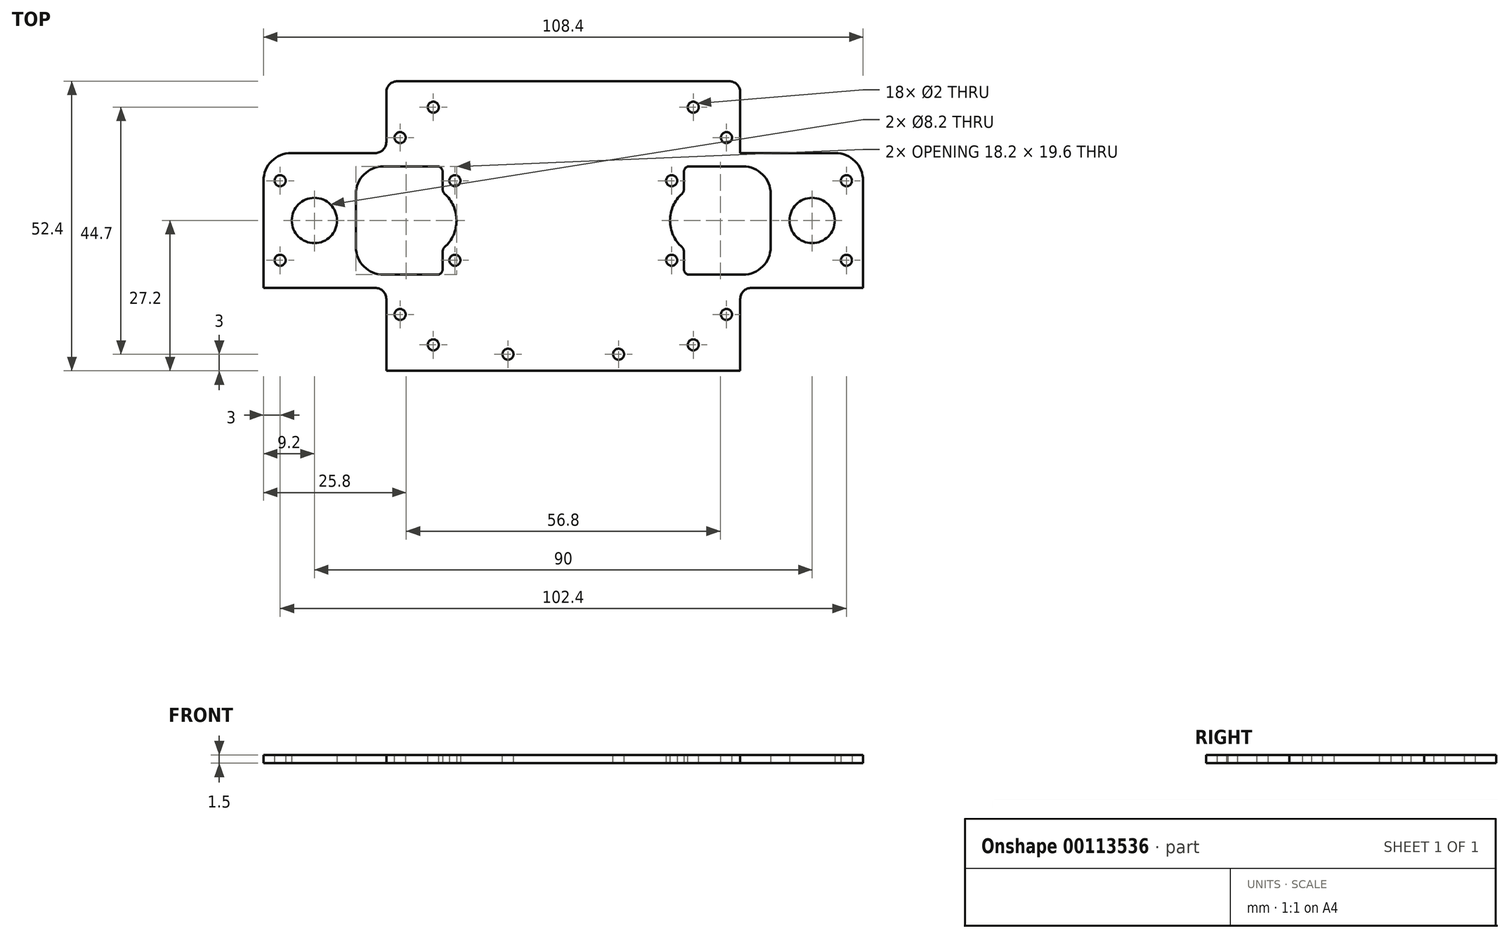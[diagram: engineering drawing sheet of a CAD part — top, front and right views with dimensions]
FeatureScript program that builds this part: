
annotation { "Feature Type Name" : "Feature", "Feature Type Description" : "" }
export const myFeature = defineFeature(function(context is Context, id is Id, definition is map)
    precondition{}
    {
        {
            var Q0;
            Q0=qCreatedBy(makeId("Top.planeOp"),FACE);
            var sketch = newSketch(context, id + "F0", { "sketchPlane" : qUnion([Q0])});
            skLineSegment(sketch, "E0.bottom", {"start": v(54.2, -12.2) * mm, "end": v(-54.2, -12.2) * mm});
            skLineSegment(sketch, "E0.top", {"start": v(54.2, 12.2) * mm, "end": v(-54.2, 12.2) * mm});
            skLineSegment(sketch, "E0.left", {"start": v(54.2, -12.2) * mm, "end": v(54.2, 12.2) * mm});
            skLineSegment(sketch, "E0.right", {"start": v(-54.2, -12.2) * mm, "end": v(-54.2, 12.2) * mm});
            skPoint(sketch, "E0.middle", {"position": v(0, 0) * mm});
            skCircle(sketch, "E1", {"center": v(-45, 0) * mm, "radius": 4.1 * mm});
            skCircle(sketch, "E2", {"center": v(-51.2, 7.2) * mm, "radius": 1 * mm});
            skCircle(sketch, "E3", {"center": v(-19.6, 7.2) * mm, "radius": 1 * mm});
            skLineSegment(sketch, "E4.bottom", {"start": v(-32.5, 9.8) * mm, "end": v(-22.8, 9.8) * mm});
            skLineSegment(sketch, "E4.top", {"start": v(-32.5, -9.8) * mm, "end": v(-22.8, -9.8) * mm});
            skLineSegment(sketch, "E4.left", {"start": v(-37.5, 4.8) * mm, "end": v(-37.5, -4.8) * mm});
            skLineSegment(sketch, "E4.right", {"start": v(-21.8, 8.8) * mm, "end": v(-21.8, 5.6) * mm});
            skPoint(sketch, "E4.middle", {"position": v(-29.65, 0) * mm});
            skPoint(sketch, "E5.visualSharp", {"position": v(-37.5, 9.8) * mm});
            skArc(sketch, "E5.filletArc", {"start": v(-32.5, 9.8) * mm, "mid": v(-36.04, 8.34) * mm, "end": v(-37.5, 4.8) * mm});
            skPoint(sketch, "E6.visualSharp", {"position": v(-37.5, -9.8) * mm});
            skArc(sketch, "E6.filletArc", {"start": v(-37.5, -4.8) * mm, "mid": v(-36.04, -8.34) * mm, "end": v(-32.5, -9.8) * mm});
            skPoint(sketch, "E7.visualSharp", {"position": v(-21.8, 9.8) * mm});
            skArc(sketch, "E7.filletArc", {"start": v(-21.8, 8.8) * mm, "mid": v(-22.1, 9.5) * mm, "end": v(-22.8, 9.8) * mm});
            skPoint(sketch, "E8.visualSharp", {"position": v(-21.8, -9.8) * mm});
            skArc(sketch, "E8.filletArc", {"start": v(-22.8, -9.8) * mm, "mid": v(-22.1, -9.5) * mm, "end": v(-21.8, -8.8) * mm});
            skCircle(sketch, "E9.MirrorC", {"center": v(-51.2, -7.2) * mm, "radius": 1 * mm});
            skCircle(sketch, "E10.MirrorC", {"center": v(-19.6, -7.2) * mm, "radius": 1 * mm});
            skArc(sketch, "E11.MirrorCS", {"start": v(21.8, 8.8) * mm, "mid": v(22.1, 9.5) * mm, "end": v(22.8, 9.8) * mm});
            skArc(sketch, "E12.MirrorCS", {"start": v(22.8, -9.8) * mm, "mid": v(22.1, -9.5) * mm, "end": v(21.8, -8.8) * mm});
            skCircle(sketch, "E13.MirrorC", {"center": v(19.6, -7.2) * mm, "radius": 1 * mm});
            skArc(sketch, "E14.MirrorCS", {"start": v(37.5, -4.8) * mm, "mid": v(36.04, -8.34) * mm, "end": v(32.5, -9.8) * mm});
            skArc(sketch, "E15.MirrorCS", {"start": v(32.5, 9.8) * mm, "mid": v(36.04, 8.34) * mm, "end": v(37.5, 4.8) * mm});
            skLineSegment(sketch, "E16.MirrorCS", {"start": v(21.8, 8.8) * mm, "end": v(21.8, 5.6) * mm});
            skPoint(sketch, "E17.MirrorP", {"position": v(21.8, -9.8) * mm});
            skLineSegment(sketch, "E18.MirrorCS", {"start": v(32.5, 9.8) * mm, "end": v(22.8, 9.8) * mm});
            skCircle(sketch, "E19.MirrorC", {"center": v(19.6, 7.2) * mm, "radius": 1 * mm});
            skPoint(sketch, "E20.MirrorP", {"position": v(21.8, 9.8) * mm});
            skPoint(sketch, "E21.MirrorP", {"position": v(29.65, 0) * mm});
            skCircle(sketch, "E22.MirrorC", {"center": v(51.2, -7.2) * mm, "radius": 1 * mm});
            skCircle(sketch, "E23.MirrorC", {"center": v(51.2, 7.2) * mm, "radius": 1 * mm});
            skCircle(sketch, "E24.MirrorC", {"center": v(45, 0) * mm, "radius": 4.1 * mm});
            skLineSegment(sketch, "E25.MirrorCS", {"start": v(37.5, 4.8) * mm, "end": v(37.5, -4.8) * mm});
            skPoint(sketch, "E26.MirrorP", {"position": v(37.5, -9.8) * mm});
            skLineSegment(sketch, "E27.MirrorCS", {"start": v(32.5, -9.8) * mm, "end": v(22.8, -9.8) * mm});
            skPoint(sketch, "E28.MirrorP", {"position": v(37.5, 9.8) * mm});
            skArc(sketch, "E29", {"start": v(-21.47, -4.84) * mm, "mid": v(-19.3, 0) * mm, "end": v(-21.47, 4.84) * mm});
            skLineSegment(sketch, "E30.trimOffspring", {"start": v(-21.8, -5.6) * mm, "end": v(-21.8, -8.8) * mm});
            skPoint(sketch, "E31.visualSharp", {"position": v(-21.8, 5.12) * mm});
            skArc(sketch, "E31.filletArc", {"start": v(-21.8, 5.6) * mm, "mid": v(-21.71, 5.18) * mm, "end": v(-21.47, 4.84) * mm});
            skPoint(sketch, "E32.visualSharp", {"position": v(-21.8, -5.12) * mm});
            skArc(sketch, "E32.filletArc", {"start": v(-21.47, -4.84) * mm, "mid": v(-21.71, -5.18) * mm, "end": v(-21.8, -5.6) * mm});
            skArc(sketch, "E33.MirrorCS", {"start": v(21.8, 5.6) * mm, "mid": v(21.71, 5.18) * mm, "end": v(21.47, 4.84) * mm});
            skArc(sketch, "E34.MirrorCS", {"start": v(21.47, -4.84) * mm, "mid": v(19.3, 0) * mm, "end": v(21.47, 4.84) * mm});
            skPoint(sketch, "E35.MirrorP", {"position": v(21.8, 5.12) * mm});
            skPoint(sketch, "E36.MirrorP", {"position": v(21.8, -5.12) * mm});
            skArc(sketch, "E37.MirrorCS", {"start": v(21.47, -4.84) * mm, "mid": v(21.71, -5.18) * mm, "end": v(21.8, -5.6) * mm});
            skLineSegment(sketch, "E38.trimOffspring", {"start": v(21.8, -5.6) * mm, "end": v(21.8, -8.8) * mm});
            skSolve(sketch);
        }
        {
            var Q0;
            Q0=qSketchRegion(id+"F0",true);
            extrude(context, id + "F1", {"entities" : qUnion([Q0]), "depth" : 1.5 * mm});
        }
        {
            var Q0;
            Q0=makeQuery(id+"F1.opExtrude","SWEPT_FACE",FACE,{"disambiguationData":[OSD([sQuery(id+"F0.wireOp",EDGE,"E0.bottom")])]});
            var sketch = newSketch(context, id + "F2", { "sketchPlane" : qUnion([Q0])});
            skLineSegment(sketch, "E39.bottom", {"start": v(-54.2, 1.5) * mm, "end": v(54.2, 1.5) * mm});
            skLineSegment(sketch, "E39.top", {"start": v(-54.2, 0) * mm, "end": v(54.2, 0) * mm});
            skLineSegment(sketch, "E39.left", {"start": v(-54.2, 1.5) * mm, "end": v(-54.2, 0) * mm});
            skLineSegment(sketch, "E39.right", {"start": v(54.2, 1.5) * mm, "end": v(54.2, 0) * mm});
            skSolve(sketch);
        }
        {
            var Q0;
            Q0=qSketchRegion(id+"F2",true);
            extrude(context, id + "F3", {"entities" : qUnion([Q0]), "operationType" : NewBodyOperationType.ADD, "depth" : 15 * mm});
        }
        {
            var Q0;
            Q0=makeQuery(id+"F3.boolean.opBoolean","MERGE",FACE,{"derivedFrom":[makeQuery(id+"F1.opExtrude","CAP_FACE",FACE,{"disambiguationData":[OSD([sQuery(id+"F0.wireOp",EDGE,"E0.bottom"),sQuery(id+"F0.wireOp",EDGE,"E0.top"),sQuery(id+"F0.wireOp",EDGE,"E0.left"),sQuery(id+"F0.wireOp",EDGE,"E0.right"),sQuery(id+"F0.wireOp",EDGE,"E1"),sQuery(id+"F0.wireOp",EDGE,"E2"),sQuery(id+"F0.wireOp",EDGE,"E3"),sQuery(id+"F0.wireOp",EDGE,"E4.bottom"),sQuery(id+"F0.wireOp",EDGE,"E4.top"),sQuery(id+"F0.wireOp",EDGE,"E4.left"),sQuery(id+"F0.wireOp",EDGE,"E4.right"),sQuery(id+"F0.wireOp",EDGE,"E5.filletArc"),sQuery(id+"F0.wireOp",EDGE,"E6.filletArc"),sQuery(id+"F0.wireOp",EDGE,"E7.filletArc"),sQuery(id+"F0.wireOp",EDGE,"E8.filletArc"),sQuery(id+"F0.wireOp",EDGE,"E9.MirrorC"),sQuery(id+"F0.wireOp",EDGE,"E10.MirrorC"),sQuery(id+"F0.wireOp",EDGE,"E11.MirrorCS"),sQuery(id+"F0.wireOp",EDGE,"E12.MirrorCS"),sQuery(id+"F0.wireOp",EDGE,"E13.MirrorC"),sQuery(id+"F0.wireOp",EDGE,"E14.MirrorCS"),sQuery(id+"F0.wireOp",EDGE,"E15.MirrorCS"),sQuery(id+"F0.wireOp",EDGE,"E16.MirrorCS"),sQuery(id+"F0.wireOp",EDGE,"E18.MirrorCS"),sQuery(id+"F0.wireOp",EDGE,"E19.MirrorC"),sQuery(id+"F0.wireOp",EDGE,"E22.MirrorC"),sQuery(id+"F0.wireOp",EDGE,"E23.MirrorC"),sQuery(id+"F0.wireOp",EDGE,"E24.MirrorC"),sQuery(id+"F0.wireOp",EDGE,"E25.MirrorCS"),sQuery(id+"F0.wireOp",EDGE,"E27.MirrorCS"),sQuery(id+"F0.wireOp",EDGE,"E29"),sQuery(id+"F0.wireOp",EDGE,"E30.trimOffspring"),sQuery(id+"F0.wireOp",EDGE,"E31.filletArc"),sQuery(id+"F0.wireOp",EDGE,"E32.filletArc"),sQuery(id+"F0.wireOp",EDGE,"E33.MirrorCS"),sQuery(id+"F0.wireOp",EDGE,"E34.MirrorCS"),sQuery(id+"F0.wireOp",EDGE,"E37.MirrorCS"),sQuery(id+"F0.wireOp",EDGE,"E38.trimOffspring")])],"isStart":false}),makeQuery(id+"F3.opExtrude","SWEPT_FACE",FACE,{"disambiguationData":[OSD([sQuery(id+"F2.wireOp",EDGE,"E39.bottom")])]})]});
            var sketch = newSketch(context, id + "F4", { "sketchPlane" : qUnion([Q0])});
            skLineSegment(sketch, "E40.bottom", {"start": v(-54.2, -27.2) * mm, "end": v(-32, -27.2) * mm});
            skLineSegment(sketch, "E40.top", {"start": v(-54.2, -12.2) * mm, "end": v(-32, -12.2) * mm});
            skLineSegment(sketch, "E40.left", {"start": v(-54.2, -27.2) * mm, "end": v(-54.2, -12.2) * mm});
            skLineSegment(sketch, "E40.right", {"start": v(-32, -27.2) * mm, "end": v(-32, -12.2) * mm});
            skPoint(sketch, "E41", {"position": v(-19.6, -7.2) * mm});
            skLineSegment(sketch, "E42.MirrorCS", {"start": v(54.2, -27.2) * mm, "end": v(32, -27.2) * mm});
            skLineSegment(sketch, "E43.MirrorCS", {"start": v(54.2, -12.2) * mm, "end": v(32, -12.2) * mm});
            skLineSegment(sketch, "E44.MirrorCS", {"start": v(54.2, -27.2) * mm, "end": v(54.2, -12.2) * mm});
            skLineSegment(sketch, "E45.MirrorCS", {"start": v(32, -27.2) * mm, "end": v(32, -12.2) * mm});
            skSolve(sketch);
        }
        {
            var Q0;
            Q0=qSketchRegion(id+"F4",true);
            extrude(context, id + "F5", {"entities" : qUnion([Q0]), "operationType" : NewBodyOperationType.REMOVE, "endBound" : BoundingType.UP_TO_NEXT, "oppositeDirection" : true, "depth" : 25 * mm});
        }
        {
            var Q0;
            Q0=makeQuery(id+"F3.boolean.opBoolean","MERGE",FACE,{"derivedFrom":[makeQuery(id+"F1.opExtrude","CAP_FACE",FACE,{"disambiguationData":[OSD([sQuery(id+"F0.wireOp",EDGE,"E0.bottom"),sQuery(id+"F0.wireOp",EDGE,"E0.top"),sQuery(id+"F0.wireOp",EDGE,"E0.left"),sQuery(id+"F0.wireOp",EDGE,"E0.right"),sQuery(id+"F0.wireOp",EDGE,"E1"),sQuery(id+"F0.wireOp",EDGE,"E2"),sQuery(id+"F0.wireOp",EDGE,"E3"),sQuery(id+"F0.wireOp",EDGE,"E4.bottom"),sQuery(id+"F0.wireOp",EDGE,"E4.top"),sQuery(id+"F0.wireOp",EDGE,"E4.left"),sQuery(id+"F0.wireOp",EDGE,"E4.right"),sQuery(id+"F0.wireOp",EDGE,"E5.filletArc"),sQuery(id+"F0.wireOp",EDGE,"E6.filletArc"),sQuery(id+"F0.wireOp",EDGE,"E7.filletArc"),sQuery(id+"F0.wireOp",EDGE,"E8.filletArc"),sQuery(id+"F0.wireOp",EDGE,"E9.MirrorC"),sQuery(id+"F0.wireOp",EDGE,"E10.MirrorC"),sQuery(id+"F0.wireOp",EDGE,"E11.MirrorCS"),sQuery(id+"F0.wireOp",EDGE,"E12.MirrorCS"),sQuery(id+"F0.wireOp",EDGE,"E13.MirrorC"),sQuery(id+"F0.wireOp",EDGE,"E14.MirrorCS"),sQuery(id+"F0.wireOp",EDGE,"E15.MirrorCS"),sQuery(id+"F0.wireOp",EDGE,"E16.MirrorCS"),sQuery(id+"F0.wireOp",EDGE,"E18.MirrorCS"),sQuery(id+"F0.wireOp",EDGE,"E19.MirrorC"),sQuery(id+"F0.wireOp",EDGE,"E22.MirrorC"),sQuery(id+"F0.wireOp",EDGE,"E23.MirrorC"),sQuery(id+"F0.wireOp",EDGE,"E24.MirrorC"),sQuery(id+"F0.wireOp",EDGE,"E25.MirrorCS"),sQuery(id+"F0.wireOp",EDGE,"E27.MirrorCS"),sQuery(id+"F0.wireOp",EDGE,"E29"),sQuery(id+"F0.wireOp",EDGE,"E30.trimOffspring"),sQuery(id+"F0.wireOp",EDGE,"E31.filletArc"),sQuery(id+"F0.wireOp",EDGE,"E32.filletArc"),sQuery(id+"F0.wireOp",EDGE,"E33.MirrorCS"),sQuery(id+"F0.wireOp",EDGE,"E34.MirrorCS"),sQuery(id+"F0.wireOp",EDGE,"E37.MirrorCS"),sQuery(id+"F0.wireOp",EDGE,"E38.trimOffspring")])],"isStart":false}),makeQuery(id+"F3.opExtrude","SWEPT_FACE",FACE,{"disambiguationData":[OSD([sQuery(id+"F2.wireOp",EDGE,"E39.bottom")])]})]});
            var sketch = newSketch(context, id + "F6", { "sketchPlane" : qUnion([Q0])});
            skLineSegment(sketch, "E46.bottom", {"start": v(-32, -27.2) * mm, "end": v(32, -27.2) * mm, "construction": true});
            skLineSegment(sketch, "E46.top", {"start": v(-32, 12.2) * mm, "end": v(32, 12.2) * mm, "construction": true});
            skLineSegment(sketch, "E46.left", {"start": v(-32, -27.2) * mm, "end": v(-32, 12.2) * mm, "construction": true});
            skLineSegment(sketch, "E46.right", {"start": v(32, -27.2) * mm, "end": v(32, 12.2) * mm, "construction": true});
            skLineSegment(sketch, "E47", {"start": v(-32, -12.2) * mm, "end": v(32, -12.2) * mm, "construction": true});
            skCircle(sketch, "E48", {"center": v(-23.5, -33.7) * mm, "radius": 1 * mm, "construction": true});
            skCircle(sketch, "E49.MirrorC", {"center": v(-23.5, 9.3) * mm, "radius": 1 * mm, "construction": true});
            skCircle(sketch, "E50.MirrorC", {"center": v(23.5, 9.3) * mm, "radius": 1 * mm, "construction": true});
            skCircle(sketch, "E51.MirrorC", {"center": v(23.5, -33.7) * mm, "radius": 1 * mm, "construction": true});
            skCircle(sketch, "E52", {"center": v(-10, -24.2) * mm, "radius": 1 * mm});
            skCircle(sketch, "E53.MirrorC", {"center": v(10, -24.2) * mm, "radius": 1 * mm});
            skSolve(sketch);
        }
        {
            var Q0;
            Q0=makeQuery(id+"F5.boolean.opBoolean","COPY",EDGE,{"derivedFrom":makeQuery(id+"F5.opExtrude","SWEPT_EDGE",EDGE,{"disambiguationData":[OSD([sQuery(id+"F4.wireOp",EDGE,"E40.top"),sQuery(id+"F4.wireOp",EDGE,"E40.right")])]})});
            var Q1;
            Q1=makeQuery(id+"F5.boolean.opBoolean","COPY",EDGE,{"derivedFrom":makeQuery(id+"F5.opExtrude","SWEPT_EDGE",EDGE,{"disambiguationData":[OSD([sQuery(id+"F4.wireOp",EDGE,"E43.MirrorCS"),sQuery(id+"F4.wireOp",EDGE,"E45.MirrorCS")])]})});
            fillet(context, id + "F7", {"entities" : qUnion([Q0, Q1]), "radius" : 2 * mm, "tangentPropagation" : true, "allowEdgeOverflow" : false});
        }
        {
            var Q0;
            Q0=makeQuery(id+"F1.opExtrude","SWEPT_EDGE",EDGE,{"disambiguationData":[OSD([sQuery(id+"F0.wireOp",EDGE,"E0.top"),sQuery(id+"F0.wireOp",EDGE,"E0.right")])]});
            var Q1;
            Q1=makeQuery(id+"F5.boolean.opBoolean","COPY",EDGE,{"derivedFrom":makeQuery(id+"F5.opExtrude","SWEPT_EDGE",EDGE,{"disambiguationData":[OSD([sQuery(id+"F0.wireOp",EDGE,"E0.right"),sQuery(id+"F2.wireOp",EDGE,"E39.bottom"),sQuery(id+"F2.wireOp",EDGE,"E39.left"),sQuery(id+"F4.wireOp",EDGE,"E40.top"),sQuery(id+"F4.wireOp",EDGE,"E40.left")])]})});
            var Q2;
            Q2=makeQuery(id+"F1.opExtrude","SWEPT_EDGE",EDGE,{"disambiguationData":[OSD([sQuery(id+"F0.wireOp",EDGE,"E0.top"),sQuery(id+"F0.wireOp",EDGE,"E0.left")])]});
            var Q3;
            Q3=makeQuery(id+"F5.boolean.opBoolean","COPY",EDGE,{"derivedFrom":makeQuery(id+"F5.opExtrude","SWEPT_EDGE",EDGE,{"disambiguationData":[OSD([sQuery(id+"F0.wireOp",EDGE,"E0.left"),sQuery(id+"F2.wireOp",EDGE,"E39.bottom"),sQuery(id+"F2.wireOp",EDGE,"E39.right"),sQuery(id+"F4.wireOp",EDGE,"E43.MirrorCS"),sQuery(id+"F4.wireOp",EDGE,"E44.MirrorCS")])]})});
            fillet(context, id + "F8", {"entities" : qUnion([Q0, Q1, Q2, Q3]), "radius" : 5 * mm, "tangentPropagation" : true, "allowEdgeOverflow" : false});
        }
        {
            var Q0;
            Q0=makeQuery(id+"F1.opExtrude","SWEPT_FACE",FACE,{"disambiguationData":[OSD([sQuery(id+"F0.wireOp",EDGE,"E0.top")])]});
            var sketch = newSketch(context, id + "F9", { "sketchPlane" : qUnion([Q0])});
            skLineSegment(sketch, "E54.bottom", {"start": v(0, 0) * mm, "end": v(-32, 0) * mm});
            skLineSegment(sketch, "E54.top", {"start": v(0, 1.5) * mm, "end": v(-32, 1.5) * mm});
            skLineSegment(sketch, "E54.left", {"start": v(0, 0) * mm, "end": v(0, 1.5) * mm});
            skLineSegment(sketch, "E54.right", {"start": v(-32, 0) * mm, "end": v(-32, 1.5) * mm});
            skLineSegment(sketch, "E55.MirrorCS", {"start": v(32, 0) * mm, "end": v(32, 1.5) * mm});
            skLineSegment(sketch, "E56.MirrorCS", {"start": v(0, 0) * mm, "end": v(32, 0) * mm});
            skLineSegment(sketch, "E57.MirrorCS", {"start": v(0, 1.5) * mm, "end": v(32, 1.5) * mm});
            skSolve(sketch);
        }
        {
            var Q0;
            Q0=qSketchRegion(id+"F9",true);
            extrude(context, id + "F10", {"entities" : qUnion([Q0]), "operationType" : NewBodyOperationType.ADD, "depth" : 13 * mm});
        }
        {
            var Q0;
            Q0=qSketchRegion(id+"F6",true);
            extrude(context, id + "F11", {"entities" : qUnion([Q0]), "operationType" : NewBodyOperationType.REMOVE, "endBound" : BoundingType.UP_TO_NEXT, "oppositeDirection" : true, "depth" : 25 * mm});
        }
        {
            var Q0;
            Q0=makeQuery(id+"F10.boolean.opBoolean","MERGE",FACE,{"derivedFrom":[makeQuery(id+"F3.boolean.opBoolean","MERGE",FACE,{"derivedFrom":[makeQuery(id+"F1.opExtrude","CAP_FACE",FACE,{"disambiguationData":[OSD([sQuery(id+"F0.wireOp",EDGE,"E0.bottom"),sQuery(id+"F0.wireOp",EDGE,"E0.top"),sQuery(id+"F0.wireOp",EDGE,"E0.left"),sQuery(id+"F0.wireOp",EDGE,"E0.right"),sQuery(id+"F0.wireOp",EDGE,"E1"),sQuery(id+"F0.wireOp",EDGE,"E2"),sQuery(id+"F0.wireOp",EDGE,"E3"),sQuery(id+"F0.wireOp",EDGE,"E4.bottom"),sQuery(id+"F0.wireOp",EDGE,"E4.top"),sQuery(id+"F0.wireOp",EDGE,"E4.left"),sQuery(id+"F0.wireOp",EDGE,"E4.right"),sQuery(id+"F0.wireOp",EDGE,"E5.filletArc"),sQuery(id+"F0.wireOp",EDGE,"E6.filletArc"),sQuery(id+"F0.wireOp",EDGE,"E7.filletArc"),sQuery(id+"F0.wireOp",EDGE,"E8.filletArc"),sQuery(id+"F0.wireOp",EDGE,"E9.MirrorC"),sQuery(id+"F0.wireOp",EDGE,"E10.MirrorC"),sQuery(id+"F0.wireOp",EDGE,"E11.MirrorCS"),sQuery(id+"F0.wireOp",EDGE,"E12.MirrorCS"),sQuery(id+"F0.wireOp",EDGE,"E13.MirrorC"),sQuery(id+"F0.wireOp",EDGE,"E14.MirrorCS"),sQuery(id+"F0.wireOp",EDGE,"E15.MirrorCS"),sQuery(id+"F0.wireOp",EDGE,"E16.MirrorCS"),sQuery(id+"F0.wireOp",EDGE,"E18.MirrorCS"),sQuery(id+"F0.wireOp",EDGE,"E19.MirrorC"),sQuery(id+"F0.wireOp",EDGE,"E22.MirrorC"),sQuery(id+"F0.wireOp",EDGE,"E23.MirrorC"),sQuery(id+"F0.wireOp",EDGE,"E24.MirrorC"),sQuery(id+"F0.wireOp",EDGE,"E25.MirrorCS"),sQuery(id+"F0.wireOp",EDGE,"E27.MirrorCS"),sQuery(id+"F0.wireOp",EDGE,"E29"),sQuery(id+"F0.wireOp",EDGE,"E30.trimOffspring"),sQuery(id+"F0.wireOp",EDGE,"E31.filletArc"),sQuery(id+"F0.wireOp",EDGE,"E32.filletArc"),sQuery(id+"F0.wireOp",EDGE,"E33.MirrorCS"),sQuery(id+"F0.wireOp",EDGE,"E34.MirrorCS"),sQuery(id+"F0.wireOp",EDGE,"E37.MirrorCS"),sQuery(id+"F0.wireOp",EDGE,"E38.trimOffspring")])],"isStart":false}),makeQuery(id+"F3.opExtrude","SWEPT_FACE",FACE,{"disambiguationData":[OSD([sQuery(id+"F2.wireOp",EDGE,"E39.bottom")])]})]}),makeQuery(id+"F10.opExtrude","SWEPT_FACE",FACE,{"disambiguationData":[OSD([sQuery(id+"F9.wireOp",EDGE,"E54.top"),sQuery(id+"F9.wireOp",EDGE,"E57.MirrorCS")])]})]});
            var sketch = newSketch(context, id + "F12", { "sketchPlane" : qUnion([Q0])});
            skLineSegment(sketch, "E58", {"start": v(-32, 25.2) * mm, "end": v(-32, -27.2) * mm, "construction": true});
            skLineSegment(sketch, "E59", {"start": v(32, 25.2) * mm, "end": v(32, -27.2) * mm, "construction": true});
            skLineSegment(sketch, "E60", {"start": v(32, -27.2) * mm, "end": v(31.5, -26.76) * mm, "construction": true});
            skLineSegment(sketch, "E61", {"start": v(-32, -1) * mm, "end": v(32, -1) * mm, "construction": true});
            skCircle(sketch, "E62", {"center": v(-23.5, 20.5) * mm, "radius": 1 * mm});
            skCircle(sketch, "E63.MirrorC", {"center": v(23.5, 20.5) * mm, "radius": 1 * mm});
            skCircle(sketch, "E64.MirrorC", {"center": v(-23.5, -22.5) * mm, "radius": 1 * mm});
            skCircle(sketch, "E65.MirrorC", {"center": v(23.5, -22.5) * mm, "radius": 1 * mm});
            skCircle(sketch, "E66", {"center": v(-29.5, 15) * mm, "radius": 1 * mm});
            skCircle(sketch, "E67.MirrorC", {"center": v(-29.5, -17) * mm, "radius": 1 * mm});
            skCircle(sketch, "E68.MirrorC", {"center": v(29.5, 15) * mm, "radius": 1 * mm});
            skCircle(sketch, "E69.MirrorC", {"center": v(29.5, -17) * mm, "radius": 1 * mm});
            skSolve(sketch);
        }
        {
            var Q0;
            Q0=qSketchRegion(id+"F12",true);
            extrude(context, id + "F13", {"entities" : qUnion([Q0]), "operationType" : NewBodyOperationType.REMOVE, "endBound" : BoundingType.UP_TO_NEXT, "oppositeDirection" : true, "depth" : 25 * mm});
        }
        {
            var Q0;
            Q0=makeQuery(id+"F5.boolean.opBoolean","COPY",EDGE,{"derivedFrom":makeQuery(id+"F5.opExtrude","SWEPT_EDGE",EDGE,{"disambiguationData":[OSD([sQuery(id+"F2.wireOp",EDGE,"E39.bottom"),sQuery(id+"F4.wireOp",EDGE,"E40.bottom"),sQuery(id+"F4.wireOp",EDGE,"E40.right")])]})});
            var Q1;
            Q1=makeQuery(id+"F5.boolean.opBoolean","COPY",EDGE,{"derivedFrom":makeQuery(id+"F5.opExtrude","SWEPT_EDGE",EDGE,{"disambiguationData":[OSD([sQuery(id+"F2.wireOp",EDGE,"E39.bottom"),sQuery(id+"F4.wireOp",EDGE,"E42.MirrorCS"),sQuery(id+"F4.wireOp",EDGE,"E45.MirrorCS")])]})});
            var Q2;
            Q2=makeQuery(id+"F10.opExtrude","CAP_EDGE",EDGE,{"disambiguationData":[OSD([sQuery(id+"F9.wireOp",EDGE,"E54.right")])],"isStart":false});
            var Q3;
            Q3=makeQuery(id+"F10.opExtrude","CAP_EDGE",EDGE,{"disambiguationData":[OSD([sQuery(id+"F9.wireOp",EDGE,"E54.right")])],"isStart":true});
            var Q4;
            Q4=makeQuery(id+"F10.opExtrude","CAP_EDGE",EDGE,{"disambiguationData":[OSD([sQuery(id+"F9.wireOp",EDGE,"E55.MirrorCS")])],"isStart":true});
            var Q5;
            Q5=makeQuery(id+"F10.opExtrude","CAP_EDGE",EDGE,{"disambiguationData":[OSD([sQuery(id+"F9.wireOp",EDGE,"E55.MirrorCS")])],"isStart":false});
            fillet(context, id + "F14", {"entities" : qUnion([Q0, Q1, Q2, Q3, Q4, Q5]), "radius" : 2 * mm, "tangentPropagation" : true, "allowEdgeOverflow" : false});
        }
    });
